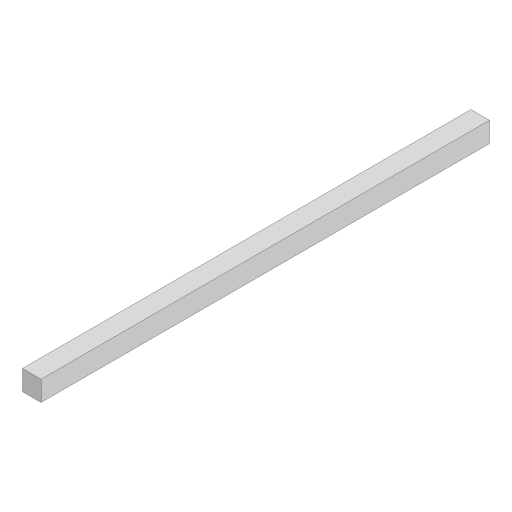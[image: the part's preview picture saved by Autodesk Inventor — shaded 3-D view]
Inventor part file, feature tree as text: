
AUTODESK INVENTOR PART (.ipt)
format: ipt  version: 2024 (Build 280153000, 153)  size: 78,336 bytes
history: native  units: in
note: dims shown in document units (in); Inventor stores cm internally (conversion verified against a paired STEP export)
features: extrude x1, sketch x1
ambient origin geometry x8: Origin, YZ Plane, XZ Plane, XY Plane, X Axis, Y Axis, Z Axis, Center Point
bodies: Solid1 (feature_tree)
feature tree (2):
  extrude  "Extrusion1"  Depth=7.0866in
  sketch  "Sketch1"  dims[d0=6.5354in d1=7.0866in d2=157.4803in d3=0.0in]
